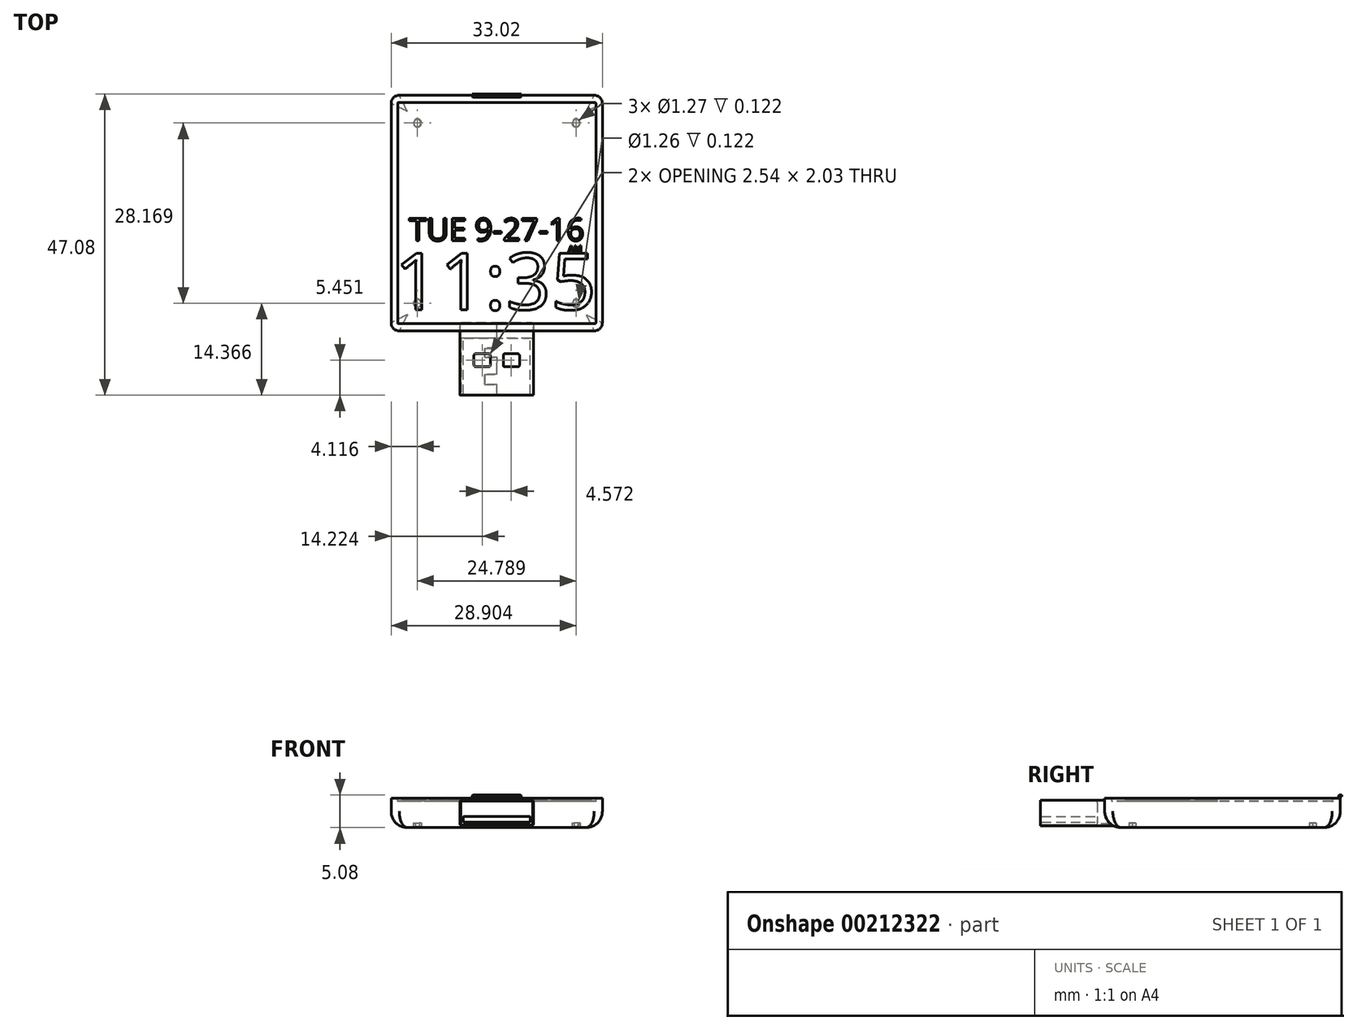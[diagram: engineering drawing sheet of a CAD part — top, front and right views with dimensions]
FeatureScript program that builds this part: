
annotation { "Feature Type Name" : "Feature", "Feature Type Description" : "" }
export const myFeature = defineFeature(function(context is Context, id is Id, definition is map)
    precondition{}
    {
        {
            var Q0;
            Q0=qCreatedBy(makeId("Top.planeOp"),FACE);
            var sketch = newSketch(context, id + "F0", { "sketchPlane" : qUnion([Q0])});
            skLineSegment(sketch, "E0.bottom", {"start": v(16.51, 18.41) * mm, "end": v(-16.51, 18.41) * mm});
            skLineSegment(sketch, "E0.top", {"start": v(16.51, -18.41) * mm, "end": v(-16.51, -18.41) * mm});
            skLineSegment(sketch, "E0.left", {"start": v(16.51, 18.41) * mm, "end": v(16.51, -18.41) * mm});
            skLineSegment(sketch, "E0.right", {"start": v(-16.51, 18.41) * mm, "end": v(-16.51, -18.41) * mm});
            skPoint(sketch, "E0.middle", {"position": v(0, 0) * mm});
            skSolve(sketch);
        }
        {
            var Q0;
            Q0=makeQuery(id+"F0.imprint","IMPRINT",FACE,{"disambiguationData":[TD([[makeQuery(id+"F0.imprint","IMPRINT",EDGE,{"derivedFrom":sQuery(id+"F0.wireOp",EDGE,"E0.bottom")}),1.0]])]});
            extrude(context, id + "F1", {"entities" : qUnion([Q0]), "depth" : 4.57 * mm});
        }
        {
            var Q0;
            Q0=makeQuery(id+"F1.opExtrude","CAP_FACE",FACE,{"disambiguationData":[OSD([sQuery(id+"F0.wireOp",EDGE,"E0.bottom"),sQuery(id+"F0.wireOp",EDGE,"E0.top"),sQuery(id+"F0.wireOp",EDGE,"E0.left"),sQuery(id+"F0.wireOp",EDGE,"E0.right")])],"isStart":false});
            var sketch = newSketch(context, id + "F2", { "sketchPlane" : qUnion([Q0])});
            skLineSegment(sketch, "E1.bottom", {"start": v(15.5, 17.27) * mm, "end": v(-15.5, 17.27) * mm});
            skLineSegment(sketch, "E1.top", {"start": v(15.5, -17.27) * mm, "end": v(-15.5, -17.27) * mm});
            skLineSegment(sketch, "E1.left", {"start": v(15.5, 17.27) * mm, "end": v(15.5, -17.27) * mm});
            skLineSegment(sketch, "E1.right", {"start": v(-15.5, 17.27) * mm, "end": v(-15.5, -17.27) * mm});
            skPoint(sketch, "E1.middle", {"position": v(0, 0) * mm});
            skSolve(sketch);
        }
        {
            var Q0;
            Q0=makeQuery(id+"F2.imprint","IMPRINT",FACE,{"disambiguationData":[TD([[makeQuery(id+"F2.imprint","IMPRINT",EDGE,{"derivedFrom":sQuery(id+"F2.wireOp",EDGE,"E1.bottom")}),1.0]])]});
            extrude(context, id + "F3", {"entities" : qUnion([Q0]), "operationType" : NewBodyOperationType.REMOVE, "oppositeDirection" : true, "depth" : 0.5 * mm});
        }
        {
            var Q0;
            Q0=makeQuery(id+"F1.opExtrude","CAP_FACE",FACE,{"disambiguationData":[OSD([sQuery(id+"F0.wireOp",EDGE,"E0.bottom"),sQuery(id+"F0.wireOp",EDGE,"E0.top"),sQuery(id+"F0.wireOp",EDGE,"E0.left"),sQuery(id+"F0.wireOp",EDGE,"E0.right")])],"isStart":false});
            var sketch = newSketch(context, id + "F4", { "sketchPlane" : qUnion([Q0])});
            skLineSegment(sketch, "E2.bottom", {"start": v(3.81, 18.12) * mm, "end": v(-3.81, 18.12) * mm});
            skLineSegment(sketch, "E2.left", {"start": v(3.81, 18.12) * mm, "end": v(3.81, 18.41) * mm});
            skLineSegment(sketch, "E2.right", {"start": v(-3.81, 18.12) * mm, "end": v(-3.81, 18.41) * mm});
            skPoint(sketch, "E2.middle", {"position": v(0, 18.41) * mm});
            skLineSegment(sketch, "E3", {"start": v(-3.81, 18.41) * mm, "end": v(3.81, 18.41) * mm});
            skSolve(sketch);
        }
        {
            var Q0;
            Q0=makeQuery(id+"F4.imprint","IMPRINT",FACE,{"disambiguationData":[TD([[makeQuery(id+"F4.imprint","IMPRINT",EDGE,{"derivedFrom":sQuery(id+"F4.wireOp",EDGE,"E2.bottom")}),-1.0]])]});
            extrude(context, id + "F5", {"entities" : qUnion([Q0]), "operationType" : NewBodyOperationType.ADD, "depth" : 0.5 * mm});
        }
        {
            var Q0;
            Q0=makeQuery(id+"F5.boolean.opBoolean","MERGE",FACE,{"derivedFrom":[makeQuery(id+"F1.opExtrude","SWEPT_FACE",FACE,{"disambiguationData":[OSD([sQuery(id+"F0.wireOp",EDGE,"E0.bottom")])]}),makeQuery(id+"F5.opExtrude","SWEPT_FACE",FACE,{"disambiguationData":[OSD([sQuery(id+"F4.wireOp",EDGE,"E3")])]})]});
            var sketch = newSketch(context, id + "F6", { "sketchPlane" : qUnion([Q0])});
            skLineSegment(sketch, "E4.bottom", {"start": v(-3.81, 5.08) * mm, "end": v(3.81, 5.08) * mm});
            skLineSegment(sketch, "E4.top", {"start": v(-3.81, 4.83) * mm, "end": v(3.81, 4.83) * mm});
            skLineSegment(sketch, "E4.left", {"start": v(-3.81, 5.08) * mm, "end": v(-3.81, 4.83) * mm});
            skLineSegment(sketch, "E4.right", {"start": v(3.81, 5.08) * mm, "end": v(3.81, 4.83) * mm});
            skSolve(sketch);
        }
        {
            var Q0;
            Q0=makeQuery(id+"F6.imprint","IMPRINT",FACE,{"disambiguationData":[TD([[makeQuery(id+"F6.imprint","IMPRINT",EDGE,{"derivedFrom":sQuery(id+"F6.wireOp",EDGE,"E4.bottom")}),-1.0]])]});
            extrude(context, id + "F7", {"entities" : qUnion([Q0]), "operationType" : NewBodyOperationType.ADD, "depth" : 0.2 * mm});
        }
        {
            var Q0;
            Q0=makeQuery(id+"F5.opExtrude","CAP_EDGE",EDGE,{"disambiguationData":[OSD([sQuery(id+"F4.wireOp",EDGE,"E2.bottom")])],"isStart":false});
            var Q1;
            Q1=makeQuery(id+"F7.boolean.opBoolean","MERGE",EDGE,{"derivedFrom":[makeQuery(id+"F5.opExtrude","CAP_EDGE",EDGE,{"disambiguationData":[OSD([sQuery(id+"F4.wireOp",EDGE,"E2.left")])],"isStart":false}),makeQuery(id+"F7.opExtrude","SWEPT_EDGE",EDGE,{"disambiguationData":[OSD([sQuery(id+"F6.wireOp",EDGE,"E4.bottom"),sQuery(id+"F6.wireOp",EDGE,"E4.left")])]})]});
            var Q2;
            Q2=makeQuery(id+"F5.opExtrude","SWEPT_EDGE",EDGE,{"disambiguationData":[OSD([sQuery(id+"F4.wireOp",EDGE,"E2.bottom"),sQuery(id+"F4.wireOp",EDGE,"E2.left")])]});
            var Q3;
            Q3=makeQuery(id+"F7.boolean.opBoolean","MERGE",EDGE,{"derivedFrom":[makeQuery(id+"F5.opExtrude","CAP_EDGE",EDGE,{"disambiguationData":[OSD([sQuery(id+"F4.wireOp",EDGE,"E2.right")])],"isStart":false}),makeQuery(id+"F7.opExtrude","SWEPT_EDGE",EDGE,{"disambiguationData":[OSD([sQuery(id+"F6.wireOp",EDGE,"E4.bottom"),sQuery(id+"F6.wireOp",EDGE,"E4.right")])]})]});
            var Q4;
            Q4=makeQuery(id+"F5.opExtrude","SWEPT_EDGE",EDGE,{"disambiguationData":[OSD([sQuery(id+"F4.wireOp",EDGE,"E2.bottom"),sQuery(id+"F4.wireOp",EDGE,"E2.right")])]});
            chamfer(context, id + "F8", {"entities" : qUnion([Q0, Q1, Q2, Q3, Q4]), "width" : 0.13 * mm, "tangentPropagation" : true});
        }
        {
            var Q0;
            Q0=makeQuery(id+"F1.opExtrude","SWEPT_FACE",FACE,{"disambiguationData":[OSD([sQuery(id+"F0.wireOp",EDGE,"E0.top")])]});
            var sketch = newSketch(context, id + "F9", { "sketchPlane" : qUnion([Q0])});
            skLineSegment(sketch, "E5.bottom", {"start": v(5.74, 0.3) * mm, "end": v(-5.74, 0.3) * mm});
            skLineSegment(sketch, "E5.top", {"start": v(5.74, 4.27) * mm, "end": v(-5.74, 4.27) * mm});
            skLineSegment(sketch, "E5.left", {"start": v(5.74, 0.3) * mm, "end": v(5.74, 4.27) * mm});
            skLineSegment(sketch, "E5.right", {"start": v(-5.74, 0.3) * mm, "end": v(-5.74, 4.27) * mm});
            skPoint(sketch, "E5.middle", {"position": v(0, 2.29) * mm});
            skPoint(sketch, "E6.orphan", {"position": v(0, 4.57) * mm});
            skPoint(sketch, "E7.start.orphan", {"position": v(0, 0) * mm});
            skSolve(sketch);
        }
        {
            var Q0;
            Q0=makeQuery(id+"F9.imprint","IMPRINT",FACE,{"disambiguationData":[TD([[makeQuery(id+"F9.imprint","IMPRINT",EDGE,{"derivedFrom":sQuery(id+"F9.wireOp",EDGE,"E5.bottom")}),-1.0]])]});
            extrude(context, id + "F10", {"entities" : qUnion([Q0]), "operationType" : NewBodyOperationType.ADD, "depth" : 10.03 * mm});
        }
        {
            var Q0;
            Q0=makeQuery(id+"F10.opExtrude","CAP_FACE",FACE,{"disambiguationData":[OSD([sQuery(id+"F9.wireOp",EDGE,"E5.bottom"),sQuery(id+"F9.wireOp",EDGE,"E5.top"),sQuery(id+"F9.wireOp",EDGE,"E5.left"),sQuery(id+"F9.wireOp",EDGE,"E5.right")])],"isStart":false});
            var sketch = newSketch(context, id + "F11", { "sketchPlane" : qUnion([Q0])});
            skLineSegment(sketch, "E8", {"start": v(0, 4.27) * mm, "end": v(0, 4.15) * mm});
            skLineSegment(sketch, "E9.bottom", {"start": v(5.61, 4.15) * mm, "end": v(-5.61, 4.15) * mm});
            skLineSegment(sketch, "E9.top", {"start": v(5.61, 0.42) * mm, "end": v(-5.61, 0.42) * mm});
            skLineSegment(sketch, "E9.left", {"start": v(5.61, 4.15) * mm, "end": v(5.61, 0.42) * mm});
            skLineSegment(sketch, "E9.right", {"start": v(-5.61, 4.15) * mm, "end": v(-5.61, 0.42) * mm});
            skPoint(sketch, "E9.middle", {"position": v(0, 2.29) * mm});
            skLineSegment(sketch, "E10.trimOffspring", {"start": v(0, 0.42) * mm, "end": v(0, 0.3) * mm});
            skSolve(sketch);
        }
        {
            var Q0;
            {var subQ0=sQuery(id+"F11.wireOp",EDGE,"E9.left");Q0=makeQuery(id+"F11.imprint","IMPRINT",FACE,{"disambiguationData":[TD([[makeQuery(id+"F11.imprint","IMPRINT",EDGE,{"derivedFrom":subQ0}),-1.0]])]});}
            extrude(context, id + "F12", {"entities" : qUnion([Q0]), "operationType" : NewBodyOperationType.REMOVE, "oppositeDirection" : true, "depth" : 8.9 * mm});
        }
        {
            var Q0;
            Q0=makeQuery(id+"F10.opExtrude","SWEPT_EDGE",EDGE,{"disambiguationData":[OSD([sQuery(id+"F9.wireOp",EDGE,"E5.top"),sQuery(id+"F9.wireOp",EDGE,"E5.right")])]});
            var Q1;
            Q1=makeQuery(id+"F12.boolean.opBoolean","COPY",EDGE,{"derivedFrom":makeQuery(id+"F12.opExtrude","SWEPT_EDGE",EDGE,{"disambiguationData":[OSD([sQuery(id+"F11.wireOp",EDGE,"E9.bottom"),sQuery(id+"F11.wireOp",EDGE,"E9.right")])]})});
            var Q2;
            Q2=makeQuery(id+"F10.opExtrude","SWEPT_EDGE",EDGE,{"disambiguationData":[OSD([sQuery(id+"F9.wireOp",EDGE,"E5.top"),sQuery(id+"F9.wireOp",EDGE,"E5.left")])]});
            var Q3;
            Q3=makeQuery(id+"F12.boolean.opBoolean","COPY",EDGE,{"derivedFrom":makeQuery(id+"F12.opExtrude","SWEPT_EDGE",EDGE,{"disambiguationData":[OSD([sQuery(id+"F11.wireOp",EDGE,"E9.top"),sQuery(id+"F11.wireOp",EDGE,"E9.left")])]})});
            var Q4;
            Q4=makeQuery(id+"F12.boolean.opBoolean","COPY",EDGE,{"derivedFrom":makeQuery(id+"F12.opExtrude","SWEPT_EDGE",EDGE,{"disambiguationData":[OSD([sQuery(id+"F11.wireOp",EDGE,"E9.top"),sQuery(id+"F11.wireOp",EDGE,"E9.right")])]})});
            var Q5;
            Q5=makeQuery(id+"F10.opExtrude","SWEPT_EDGE",EDGE,{"disambiguationData":[OSD([sQuery(id+"F9.wireOp",EDGE,"E5.bottom"),sQuery(id+"F9.wireOp",EDGE,"E5.right")])]});
            var Q6;
            Q6=makeQuery(id+"F10.opExtrude","SWEPT_EDGE",EDGE,{"disambiguationData":[OSD([sQuery(id+"F9.wireOp",EDGE,"E5.bottom"),sQuery(id+"F9.wireOp",EDGE,"E5.left")])]});
            var Q7;
            Q7=makeQuery(id+"F12.boolean.opBoolean","COPY",EDGE,{"derivedFrom":makeQuery(id+"F12.opExtrude","SWEPT_EDGE",EDGE,{"disambiguationData":[OSD([sQuery(id+"F11.wireOp",EDGE,"E9.bottom"),sQuery(id+"F11.wireOp",EDGE,"E9.left")])]})});
            fillet(context, id + "F13", {"entities" : qUnion([Q0, Q1, Q2, Q3, Q4, Q5, Q6, Q7]), "radius" : 0.26 * mm, "tangentPropagation" : true, "allowEdgeOverflow" : false});
        }
        {
            var Q0;
            Q0=makeQuery(id+"F12.boolean.opBoolean","COPY",FACE,{"derivedFrom":makeQuery(id+"F12.opExtrude","CAP_FACE",FACE,{"disambiguationData":[OSD([sQuery(id+"F11.wireOp",EDGE,"E9.bottom"),sQuery(id+"F11.wireOp",EDGE,"E9.top"),sQuery(id+"F11.wireOp",EDGE,"E9.left"),sQuery(id+"F11.wireOp",EDGE,"E9.right")])],"isStart":false})});
            var sketch = newSketch(context, id + "F14", { "sketchPlane" : qUnion([Q0])});
            skLineSegment(sketch, "E11.bottom", {"start": v(-5.22, 1.74) * mm, "end": v(5.22, 1.74) * mm});
            skLineSegment(sketch, "E11.top", {"start": v(-5.22, 0.86) * mm, "end": v(5.22, 0.86) * mm});
            skLineSegment(sketch, "E11.left", {"start": v(-5.22, 1.74) * mm, "end": v(-5.22, 0.86) * mm});
            skLineSegment(sketch, "E11.right", {"start": v(5.22, 1.74) * mm, "end": v(5.22, 0.86) * mm});
            skSolve(sketch);
        }
        {
            var Q0;
            Q0=makeQuery(id+"F14.imprint","IMPRINT",FACE,{"disambiguationData":[TD([[makeQuery(id+"F14.imprint","IMPRINT",EDGE,{"derivedFrom":sQuery(id+"F14.wireOp",EDGE,"E11.bottom")}),-1.0]])]});
            extrude(context, id + "F15", {"entities" : qUnion([Q0]), "operationType" : NewBodyOperationType.ADD, "depth" : 8.9 * mm});
        }
        {
            var Q0;
            Q0=makeQuery(id+"F10.opExtrude","SWEPT_FACE",FACE,{"disambiguationData":[OSD([sQuery(id+"F9.wireOp",EDGE,"E5.top")])]});
            var sketch = newSketch(context, id + "F16", { "sketchPlane" : qUnion([Q0])});
            skLineSegment(sketch, "E12.bottom", {"start": v(-3.56, -21.98) * mm, "end": v(-1.02, -21.98) * mm});
            skLineSegment(sketch, "E12.top", {"start": v(-3.56, -24.02) * mm, "end": v(-1.02, -24.02) * mm});
            skLineSegment(sketch, "E12.left", {"start": v(-3.56, -21.98) * mm, "end": v(-3.56, -24.02) * mm});
            skLineSegment(sketch, "E12.right", {"start": v(-1.02, -21.98) * mm, "end": v(-1.02, -24.02) * mm});
            skLineSegment(sketch, "E13.bottom", {"start": v(1.02, -21.98) * mm, "end": v(3.56, -21.98) * mm});
            skLineSegment(sketch, "E13.top", {"start": v(1.02, -24.02) * mm, "end": v(3.56, -24.02) * mm});
            skLineSegment(sketch, "E13.left", {"start": v(1.02, -21.98) * mm, "end": v(1.02, -24.02) * mm});
            skLineSegment(sketch, "E13.right", {"start": v(3.56, -21.98) * mm, "end": v(3.56, -24.02) * mm});
            skSolve(sketch);
        }
        {
            var Q0;
            Q0=makeQuery(id+"F16.imprint","IMPRINT",FACE,{"disambiguationData":[TD([[makeQuery(id+"F16.imprint","IMPRINT",EDGE,{"derivedFrom":sQuery(id+"F16.wireOp",EDGE,"E13.bottom")}),-1.0]])]});
            var Q1;
            Q1=makeQuery(id+"F16.imprint","IMPRINT",FACE,{"disambiguationData":[TD([[makeQuery(id+"F16.imprint","IMPRINT",EDGE,{"derivedFrom":sQuery(id+"F16.wireOp",EDGE,"E12.bottom")}),-1.0]])]});
            extrude(context, id + "F17", {"entities" : qUnion([Q0, Q1]), "operationType" : NewBodyOperationType.REMOVE, "oppositeDirection" : true, "depth" : 0.33 * mm});
        }
        {
            var Q0;
            Q0=makeQuery(id+"F17.boolean.opBoolean","COPY",EDGE,{"derivedFrom":makeQuery(id+"F17.opExtrude","SWEPT_EDGE",EDGE,{"disambiguationData":[OSD([sQuery(id+"F16.wireOp",EDGE,"E13.bottom"),sQuery(id+"F16.wireOp",EDGE,"E13.left")])]})});
            var Q1;
            Q1=makeQuery(id+"F17.boolean.opBoolean","COPY",EDGE,{"derivedFrom":makeQuery(id+"F17.opExtrude","SWEPT_EDGE",EDGE,{"disambiguationData":[OSD([sQuery(id+"F16.wireOp",EDGE,"E12.bottom"),sQuery(id+"F16.wireOp",EDGE,"E12.left")])]})});
            var Q2;
            Q2=makeQuery(id+"F17.boolean.opBoolean","COPY",EDGE,{"derivedFrom":makeQuery(id+"F17.opExtrude","SWEPT_EDGE",EDGE,{"disambiguationData":[OSD([sQuery(id+"F16.wireOp",EDGE,"E12.bottom"),sQuery(id+"F16.wireOp",EDGE,"E12.right")])]})});
            var Q3;
            Q3=makeQuery(id+"F17.boolean.opBoolean","COPY",EDGE,{"derivedFrom":makeQuery(id+"F17.opExtrude","SWEPT_EDGE",EDGE,{"disambiguationData":[OSD([sQuery(id+"F16.wireOp",EDGE,"E13.bottom"),sQuery(id+"F16.wireOp",EDGE,"E13.right")])]})});
            var Q4;
            Q4=makeQuery(id+"F17.boolean.opBoolean","COPY",EDGE,{"derivedFrom":makeQuery(id+"F17.opExtrude","SWEPT_EDGE",EDGE,{"disambiguationData":[OSD([sQuery(id+"F16.wireOp",EDGE,"E13.top"),sQuery(id+"F16.wireOp",EDGE,"E13.right")])]})});
            var Q5;
            Q5=makeQuery(id+"F17.boolean.opBoolean","COPY",EDGE,{"derivedFrom":makeQuery(id+"F17.opExtrude","SWEPT_EDGE",EDGE,{"disambiguationData":[OSD([sQuery(id+"F16.wireOp",EDGE,"E12.top"),sQuery(id+"F16.wireOp",EDGE,"E12.right")])]})});
            var Q6;
            Q6=makeQuery(id+"F17.boolean.opBoolean","COPY",EDGE,{"derivedFrom":makeQuery(id+"F17.opExtrude","SWEPT_EDGE",EDGE,{"disambiguationData":[OSD([sQuery(id+"F16.wireOp",EDGE,"E12.top"),sQuery(id+"F16.wireOp",EDGE,"E12.left")])]})});
            var Q7;
            Q7=makeQuery(id+"F17.boolean.opBoolean","COPY",EDGE,{"derivedFrom":makeQuery(id+"F17.opExtrude","SWEPT_EDGE",EDGE,{"disambiguationData":[OSD([sQuery(id+"F16.wireOp",EDGE,"E13.top"),sQuery(id+"F16.wireOp",EDGE,"E13.left")])]})});
            fillet(context, id + "F18", {"entities" : qUnion([Q0, Q1, Q2, Q3, Q4, Q5, Q6, Q7]), "radius" : 0.25 * mm, "tangentPropagation" : true, "allowEdgeOverflow" : false});
        }
        {
            var Q0;
            Q0=makeQuery(id+"F15.opExtrude","SWEPT_EDGE",EDGE,{"disambiguationData":[OSD([sQuery(id+"F14.wireOp",EDGE,"E11.bottom"),sQuery(id+"F14.wireOp",EDGE,"E11.left")])]});
            var Q1;
            Q1=makeQuery(id+"F15.opExtrude","SWEPT_EDGE",EDGE,{"disambiguationData":[OSD([sQuery(id+"F14.wireOp",EDGE,"E11.bottom"),sQuery(id+"F14.wireOp",EDGE,"E11.right")])]});
            var Q2;
            Q2=makeQuery(id+"F15.opExtrude","SWEPT_EDGE",EDGE,{"disambiguationData":[OSD([sQuery(id+"F14.wireOp",EDGE,"E11.top"),sQuery(id+"F14.wireOp",EDGE,"E11.right")])]});
            var Q3;
            Q3=makeQuery(id+"F15.opExtrude","SWEPT_EDGE",EDGE,{"disambiguationData":[OSD([sQuery(id+"F14.wireOp",EDGE,"E11.top"),sQuery(id+"F14.wireOp",EDGE,"E11.left")])]});
            var Q4;
            Q4=makeQuery(id+"F15.opExtrude","CAP_EDGE",EDGE,{"disambiguationData":[OSD([sQuery(id+"F14.wireOp",EDGE,"E11.bottom")])],"isStart":false});
            var Q5;
            Q5=makeQuery(id+"F15.opExtrude","CAP_EDGE",EDGE,{"disambiguationData":[OSD([sQuery(id+"F14.wireOp",EDGE,"E11.top")])],"isStart":false});
            var Q6;
            Q6=makeQuery(id+"F15.opExtrude","CAP_EDGE",EDGE,{"disambiguationData":[OSD([sQuery(id+"F14.wireOp",EDGE,"E11.left")])],"isStart":false});
            var Q7;
            Q7=makeQuery(id+"F15.opExtrude","CAP_EDGE",EDGE,{"disambiguationData":[OSD([sQuery(id+"F14.wireOp",EDGE,"E11.right")])],"isStart":false});
            fillet(context, id + "F19", {"entities" : qUnion([Q0, Q1, Q2, Q3, Q4, Q5, Q6, Q7]), "radius" : 0.13 * mm, "tangentPropagation" : true, "allowEdgeOverflow" : false});
        }
        {
            var Q0;
            Q0=makeQuery(id+"F10.opExtrude","SWEPT_FACE",FACE,{"disambiguationData":[OSD([sQuery(id+"F9.wireOp",EDGE,"E5.bottom")])]});
            var sketch = newSketch(context, id + "F20", { "sketchPlane" : qUnion([Q0])});
            skLineSegment(sketch, "E14", {"start": v(0, 28.45) * mm, "end": v(0, 26.77) * mm});
            skLineSegment(sketch, "E15", {"start": v(0, 26.77) * mm, "end": v(-1.86, 26.77) * mm});
            skLineSegment(sketch, "E16", {"start": v(-1.86, 26.77) * mm, "end": v(-1.86, 25.2) * mm});
            skLineSegment(sketch, "E17", {"start": v(-1.86, 25.2) * mm, "end": v(0, 25.2) * mm});
            skLineSegment(sketch, "E18", {"start": v(0, 25.2) * mm, "end": v(0, 22.54) * mm});
            skLineSegment(sketch, "E19", {"start": v(0, 22.54) * mm, "end": v(-1.86, 22.54) * mm});
            skLineSegment(sketch, "E20", {"start": v(-1.86, 22.54) * mm, "end": v(-1.86, 21.11) * mm});
            skLineSegment(sketch, "E21", {"start": v(-1.86, 21.11) * mm, "end": v(0, 21.11) * mm});
            skLineSegment(sketch, "E22", {"start": v(0, 21.11) * mm, "end": v(0, 18.41) * mm});
            skLineSegment(sketch, "E23", {"start": v(0, 18.41) * mm, "end": v(0, 18.41) * mm});
            skLineSegment(sketch, "E24", {"start": v(0, 18.41) * mm, "end": v(0, 21.1) * mm});
            skLineSegment(sketch, "E25", {"start": v(0, 21.1) * mm, "end": v(-1.86, 21.1) * mm});
            skLineSegment(sketch, "E26", {"start": v(-1.86, 21.1) * mm, "end": v(-1.86, 22.54) * mm});
            skLineSegment(sketch, "E27", {"start": v(-1.86, 22.54) * mm, "end": v(0, 22.54) * mm});
            skLineSegment(sketch, "E28", {"start": v(0, 22.54) * mm, "end": v(0, 25.2) * mm});
            skLineSegment(sketch, "E29", {"start": v(0, 25.2) * mm, "end": v(-1.86, 25.2) * mm});
            skLineSegment(sketch, "E30", {"start": v(-1.86, 25.2) * mm, "end": v(-1.86, 26.77) * mm});
            skLineSegment(sketch, "E31", {"start": v(-1.86, 26.77) * mm, "end": v(0, 26.77) * mm});
            skLineSegment(sketch, "E32", {"start": v(0, 26.77) * mm, "end": v(0, 28.45) * mm});
            skLineSegment(sketch, "E33", {"start": v(0, 28.45) * mm, "end": v(0, 28.45) * mm});
            skSolve(sketch);
        }
        {
            var Q0;
            Q0=makeQuery(id+"F20.imprint","IMPRINT",FACE,{"disambiguationData":[TD([[makeQuery(id+"F20.imprint","IMPRINT",EDGE,{"derivedFrom":sQuery(id+"F20.wireOp",EDGE,"E14")}),-1.0]])]});
            extrude(context, id + "F21", {"entities" : qUnion([Q0]), "operationType" : NewBodyOperationType.REMOVE, "oppositeDirection" : true, "depth" : 0.27 * mm});
        }
        {
            var Q0;
            Q0=makeQuery(id+"F3.boolean.opBoolean","COPY",EDGE,{"derivedFrom":makeQuery(id+"F3.opExtrude","CAP_EDGE",EDGE,{"disambiguationData":[OSD([sQuery(id+"F2.wireOp",EDGE,"E1.top")])],"isStart":true})});
            var Q1;
            Q1=makeQuery(id+"F3.boolean.opBoolean","COPY",EDGE,{"derivedFrom":makeQuery(id+"F3.opExtrude","CAP_EDGE",EDGE,{"disambiguationData":[OSD([sQuery(id+"F2.wireOp",EDGE,"E1.left")])],"isStart":true})});
            var Q2;
            Q2=makeQuery(id+"F3.boolean.opBoolean","COPY",EDGE,{"derivedFrom":makeQuery(id+"F3.opExtrude","CAP_EDGE",EDGE,{"disambiguationData":[OSD([sQuery(id+"F2.wireOp",EDGE,"E1.bottom")])],"isStart":true})});
            var Q3;
            Q3=makeQuery(id+"F3.boolean.opBoolean","COPY",EDGE,{"derivedFrom":makeQuery(id+"F3.opExtrude","CAP_EDGE",EDGE,{"disambiguationData":[OSD([sQuery(id+"F2.wireOp",EDGE,"E1.right")])],"isStart":true})});
            var Q4;
            Q4=makeQuery(id+"F3.boolean.opBoolean","COPY",EDGE,{"derivedFrom":makeQuery(id+"F3.opExtrude","SWEPT_EDGE",EDGE,{"disambiguationData":[OSD([sQuery(id+"F2.wireOp",EDGE,"E1.bottom"),sQuery(id+"F2.wireOp",EDGE,"E1.right")])]})});
            var Q5;
            Q5=makeQuery(id+"F3.boolean.opBoolean","COPY",EDGE,{"derivedFrom":makeQuery(id+"F3.opExtrude","SWEPT_EDGE",EDGE,{"disambiguationData":[OSD([sQuery(id+"F2.wireOp",EDGE,"E1.top"),sQuery(id+"F2.wireOp",EDGE,"E1.right")])]})});
            var Q6;
            Q6=makeQuery(id+"F3.boolean.opBoolean","COPY",EDGE,{"derivedFrom":makeQuery(id+"F3.opExtrude","SWEPT_EDGE",EDGE,{"disambiguationData":[OSD([sQuery(id+"F2.wireOp",EDGE,"E1.top"),sQuery(id+"F2.wireOp",EDGE,"E1.left")])]})});
            var Q7;
            Q7=makeQuery(id+"F3.boolean.opBoolean","COPY",EDGE,{"derivedFrom":makeQuery(id+"F3.opExtrude","SWEPT_EDGE",EDGE,{"disambiguationData":[OSD([sQuery(id+"F2.wireOp",EDGE,"E1.bottom"),sQuery(id+"F2.wireOp",EDGE,"E1.left")])]})});
            fillet(context, id + "F22", {"entities" : qUnion([Q0, Q1, Q2, Q3, Q4, Q5, Q6, Q7]), "radius" : 0.1 * mm, "tangentPropagation" : true, "allowEdgeOverflow" : false});
        }
        {
            var Q0;
            Q0=makeQuery(id+"F1.opExtrude","CAP_EDGE",EDGE,{"disambiguationData":[OSD([sQuery(id+"F0.wireOp",EDGE,"E0.left")])],"isStart":true});
            var Q1;
            Q1=makeQuery(id+"F1.opExtrude","CAP_EDGE",EDGE,{"disambiguationData":[OSD([sQuery(id+"F0.wireOp",EDGE,"E0.top")])],"isStart":true});
            var Q2;
            Q2=makeQuery(id+"F1.opExtrude","CAP_EDGE",EDGE,{"disambiguationData":[OSD([sQuery(id+"F0.wireOp",EDGE,"E0.right")])],"isStart":true});
            var Q3;
            Q3=makeQuery(id+"F1.opExtrude","CAP_EDGE",EDGE,{"disambiguationData":[OSD([sQuery(id+"F0.wireOp",EDGE,"E0.bottom")])],"isStart":true});
            fillet(context, id + "F23", {"entities" : qUnion([Q0, Q1, Q2, Q3]), "radius" : 2.54 * mm, "tangentPropagation" : true, "allowEdgeOverflow" : false});
        }
        {
            var Q0;
            Q0=makeQuery(id+"F1.opExtrude","SWEPT_EDGE",EDGE,{"disambiguationData":[OSD([sQuery(id+"F0.wireOp",EDGE,"E0.bottom"),sQuery(id+"F0.wireOp",EDGE,"E0.right")])]});
            var Q1;
            Q1=makeQuery(id+"F1.opExtrude","SWEPT_EDGE",EDGE,{"disambiguationData":[OSD([sQuery(id+"F0.wireOp",EDGE,"E0.top"),sQuery(id+"F0.wireOp",EDGE,"E0.right")])]});
            var Q2;
            Q2=makeQuery(id+"F1.opExtrude","SWEPT_EDGE",EDGE,{"disambiguationData":[OSD([sQuery(id+"F0.wireOp",EDGE,"E0.top"),sQuery(id+"F0.wireOp",EDGE,"E0.left")])]});
            var Q3;
            Q3=makeQuery(id+"F1.opExtrude","SWEPT_EDGE",EDGE,{"disambiguationData":[OSD([sQuery(id+"F0.wireOp",EDGE,"E0.bottom"),sQuery(id+"F0.wireOp",EDGE,"E0.left")])]});
            fillet(context, id + "F24", {"entities" : qUnion([Q0, Q1, Q2, Q3]), "radius" : 1.27 * mm, "tangentPropagation" : true, "allowEdgeOverflow" : false});
        }
        {
            var Q0;
            Q0=makeQuery(id+"F1.opExtrude","CAP_FACE",FACE,{"disambiguationData":[OSD([sQuery(id+"F0.wireOp",EDGE,"E0.bottom"),sQuery(id+"F0.wireOp",EDGE,"E0.top"),sQuery(id+"F0.wireOp",EDGE,"E0.left"),sQuery(id+"F0.wireOp",EDGE,"E0.right")])],"isStart":true});
            var sketch = newSketch(context, id + "F25", { "sketchPlane" : qUnion([Q0])});
            skLineSegment(sketch, "E34", {"start": v(-12.4, 14.08) * mm, "end": v(-12.4, -14.08) * mm, "construction": true});
            skLineSegment(sketch, "E35", {"start": v(-12.4, -14.08) * mm, "end": v(12.4, -14.08) * mm, "construction": true});
            skLineSegment(sketch, "E36", {"start": v(12.4, -14.08) * mm, "end": v(12.4, 14.08) * mm, "construction": true});
            skLineSegment(sketch, "E37", {"start": v(12.4, 14.08) * mm, "end": v(-12.4, 14.08) * mm, "construction": true});
            skCircle(sketch, "E38", {"center": v(-12.4, 14.08) * mm, "radius": 0.63 * mm});
            skCircle(sketch, "E39", {"center": v(12.4, 14.08) * mm, "radius": 0.63 * mm});
            skCircle(sketch, "E40", {"center": v(12.4, -14.08) * mm, "radius": 0.63 * mm});
            skCircle(sketch, "E41", {"center": v(-12.4, -14.08) * mm, "radius": 0.63 * mm});
            skSolve(sketch);
        }
        {
            var Q0;
            Q0=makeQuery(id+"F25.imprint","IMPRINT",FACE,{"disambiguationData":[TD([[makeQuery(id+"F25.imprint","IMPRINT",EDGE,{"derivedFrom":sQuery(id+"F25.wireOp",EDGE,"E41")}),1.0]])]});
            var Q1;
            Q1=makeQuery(id+"F25.imprint","IMPRINT",FACE,{"disambiguationData":[TD([[makeQuery(id+"F25.imprint","IMPRINT",EDGE,{"derivedFrom":sQuery(id+"F25.wireOp",EDGE,"E40")}),1.0]])]});
            var Q2;
            Q2=makeQuery(id+"F25.imprint","IMPRINT",FACE,{"disambiguationData":[TD([[makeQuery(id+"F25.imprint","IMPRINT",EDGE,{"derivedFrom":sQuery(id+"F25.wireOp",EDGE,"E39")}),1.0]])]});
            var Q3;
            Q3=makeQuery(id+"F25.imprint","IMPRINT",FACE,{"disambiguationData":[TD([[makeQuery(id+"F25.imprint","IMPRINT",EDGE,{"derivedFrom":sQuery(id+"F25.wireOp",EDGE,"E38")}),1.0]])]});
            extrude(context, id + "F26", {"entities" : qUnion([Q0, Q1, Q2, Q3]), "operationType" : NewBodyOperationType.REMOVE, "oppositeDirection" : true, "depth" : 0.12 * mm});
        }
        {
            var Q0;
            Q0=makeQuery(id+"F26.boolean.opBoolean","COPY",FACE,{"derivedFrom":makeQuery(id+"F26.opExtrude","CAP_FACE",FACE,{"disambiguationData":[OSD([sQuery(id+"F25.wireOp",EDGE,"E41")])],"isStart":false})});
            var sketch = newSketch(context, id + "F27", { "sketchPlane" : qUnion([Q0])});
            skCircle(sketch, "E42.cCircle", {"center": v(-12.4, -14.08) * mm, "radius": 0.54 * mm, "construction": true});
            skLineSegment(sketch, "E42.0", {"start": v(-12.7, -13.55) * mm, "end": v(-12.08, -13.55) * mm});
            skLineSegment(sketch, "E42.1", {"start": v(-12.08, -13.55) * mm, "end": v(-11.77, -14.08) * mm});
            skLineSegment(sketch, "E42.2", {"start": v(-11.77, -14.08) * mm, "end": v(-12.08, -14.62) * mm});
            skLineSegment(sketch, "E42.3", {"start": v(-12.08, -14.62) * mm, "end": v(-12.7, -14.62) * mm});
            skLineSegment(sketch, "E42.4", {"start": v(-12.7, -14.62) * mm, "end": v(-13.02, -14.08) * mm});
            skLineSegment(sketch, "E42.5", {"start": v(-13.02, -14.08) * mm, "end": v(-12.7, -13.55) * mm});
            skPoint(sketch, "E42.0.midPoint", {"position": v(-12.4, -13.55) * mm});
            skLineSegment(sketch, "E43", {"start": v(12.4, -13.45) * mm, "end": v(12.4, -14.72) * mm});
            skCircle(sketch, "E44.cCircle", {"center": v(12.4, -14.08) * mm, "radius": 0.54 * mm, "construction": true});
            skLineSegment(sketch, "E44.0", {"start": v(12.09, -13.55) * mm, "end": v(12.7, -13.55) * mm});
            skLineSegment(sketch, "E44.1", {"start": v(12.7, -13.55) * mm, "end": v(13.02, -14.08) * mm});
            skLineSegment(sketch, "E44.2", {"start": v(13.02, -14.08) * mm, "end": v(12.7, -14.62) * mm});
            skLineSegment(sketch, "E44.3", {"start": v(12.7, -14.62) * mm, "end": v(12.09, -14.62) * mm});
            skLineSegment(sketch, "E44.4", {"start": v(12.09, -14.62) * mm, "end": v(11.78, -14.08) * mm});
            skLineSegment(sketch, "E44.5", {"start": v(11.78, -14.08) * mm, "end": v(12.09, -13.55) * mm});
            skPoint(sketch, "E44.0.midPoint", {"position": v(12.4, -13.55) * mm});
            skLineSegment(sketch, "E45", {"start": v(12.38, 14.72) * mm, "end": v(12.38, 13.46) * mm});
            skCircle(sketch, "E46.cCircle", {"center": v(12.38, 14.09) * mm, "radius": 0.52 * mm, "construction": true});
            skLineSegment(sketch, "E46.0", {"start": v(12.08, 14.61) * mm, "end": v(12.68, 14.61) * mm});
            skLineSegment(sketch, "E46.1", {"start": v(12.68, 14.61) * mm, "end": v(12.99, 14.09) * mm});
            skLineSegment(sketch, "E46.2", {"start": v(12.99, 14.09) * mm, "end": v(12.68, 13.56) * mm});
            skLineSegment(sketch, "E46.3", {"start": v(12.68, 13.56) * mm, "end": v(12.08, 13.56) * mm});
            skLineSegment(sketch, "E46.4", {"start": v(12.08, 13.56) * mm, "end": v(11.78, 14.09) * mm});
            skLineSegment(sketch, "E46.5", {"start": v(11.78, 14.09) * mm, "end": v(12.08, 14.61) * mm});
            skPoint(sketch, "E46.0.midPoint", {"position": v(12.38, 14.61) * mm});
            skCircle(sketch, "E47.cCircle", {"center": v(-12.4, 14.09) * mm, "radius": 0.55 * mm, "construction": true});
            skLineSegment(sketch, "E47.0", {"start": v(-12.7, 14.63) * mm, "end": v(-12.08, 14.63) * mm});
            skLineSegment(sketch, "E47.1", {"start": v(-12.08, 14.63) * mm, "end": v(-11.76, 14.09) * mm});
            skLineSegment(sketch, "E47.2", {"start": v(-11.76, 14.09) * mm, "end": v(-12.08, 13.54) * mm});
            skLineSegment(sketch, "E47.3", {"start": v(-12.08, 13.54) * mm, "end": v(-12.7, 13.54) * mm});
            skLineSegment(sketch, "E47.4", {"start": v(-12.7, 13.54) * mm, "end": v(-13.03, 14.09) * mm});
            skLineSegment(sketch, "E47.5", {"start": v(-13.03, 14.09) * mm, "end": v(-12.7, 14.63) * mm});
            skPoint(sketch, "E47.0.midPoint", {"position": v(-12.4, 14.63) * mm});
            skSolve(sketch);
        }
        {
            var Q0;
            Q0=makeQuery(id+"F27.imprint","IMPRINT",FACE,{"disambiguationData":[TD([[makeQuery(id+"F27.imprint","IMPRINT",EDGE,{"derivedFrom":sQuery(id+"F27.wireOp",EDGE,"E47.0")}),-1.0]])]});
            var Q1;
            {var subQ0=sQuery(id+"F27.wireOp",EDGE,"E46.4");Q1=makeQuery(id+"F27.imprint","IMPRINT",FACE,{"disambiguationData":[TD([[makeQuery(id+"F27.imprint","IMPRINT",EDGE,{"derivedFrom":subQ0}),-1.0]])]});}
            var Q2;
            {var subQ1=sQuery(id+"F27.wireOp",EDGE,"E46.1");Q2=makeQuery(id+"F27.imprint","IMPRINT",FACE,{"disambiguationData":[TD([[makeQuery(id+"F27.imprint","IMPRINT",EDGE,{"derivedFrom":subQ1}),-1.0]])]});}
            var Q3;
            {var subQ1=sQuery(id+"F27.wireOp",EDGE,"E44.1");Q3=makeQuery(id+"F27.imprint","IMPRINT",FACE,{"disambiguationData":[TD([[makeQuery(id+"F27.imprint","IMPRINT",EDGE,{"derivedFrom":subQ1}),-1.0]])]});}
            var Q4;
            {var subQ0=sQuery(id+"F27.wireOp",EDGE,"E44.4");Q4=makeQuery(id+"F27.imprint","IMPRINT",FACE,{"disambiguationData":[TD([[makeQuery(id+"F27.imprint","IMPRINT",EDGE,{"derivedFrom":subQ0}),-1.0]])]});}
            var Q5;
            Q5=makeQuery(id+"F27.imprint","IMPRINT",FACE,{"disambiguationData":[TD([[makeQuery(id+"F27.imprint","IMPRINT",EDGE,{"derivedFrom":sQuery(id+"F27.wireOp",EDGE,"E42.0")}),-1.0]])]});
            extrude(context, id + "F28", {"entities" : qUnion([Q0, Q1, Q2, Q3, Q4, Q5]), "operationType" : NewBodyOperationType.REMOVE, "oppositeDirection" : true, "depth" : 0.63 * mm});
        }
        {
            var Q0;
            Q0=makeQuery(id+"F3.boolean.opBoolean","COPY",FACE,{"derivedFrom":makeQuery(id+"F3.opExtrude","CAP_FACE",FACE,{"disambiguationData":[OSD([sQuery(id+"F2.wireOp",EDGE,"E1.bottom"),sQuery(id+"F2.wireOp",EDGE,"E1.top"),sQuery(id+"F2.wireOp",EDGE,"E1.left"),sQuery(id+"F2.wireOp",EDGE,"E1.right")])],"isStart":false})});
            extrude(context, id + "F29", {"entities" : qUnion([Q0]), "depth" : 0.1 * mm});
        }
        {
            var Q0;
            Q0=makeQuery(id+"F29.opExtrude","CAP_FACE",FACE,{"disambiguationData":[OSD([sQuery(id+"F2.wireOp",EDGE,"E1.bottom"),sQuery(id+"F2.wireOp",EDGE,"E1.top"),sQuery(id+"F2.wireOp",EDGE,"E1.left"),sQuery(id+"F2.wireOp",EDGE,"E1.right")])],"isStart":false});
            var sketch = newSketch(context, id + "F30", { "sketchPlane" : qUnion([Q0])});
            skText(sketch, "E48", { "text": "11:35", "fontName": "OpenSans-Regular.ttf"});
            skText(sketch, "E49", { "text": "TUE 9-27-16", "fontName": "OpenSans-Regular.ttf"});
            skText(sketch, "E50", { "text": "AM", "fontName": "OpenSans-Regular.ttf"});
            const initialGuessF30  = {"E48": [-0.016, -0.01508, 1, 0, 0.00889], "E49": [-0.0137, -0.00432, 1, 0, 0.00352], "E50": [0.0112, -0.00607, 1, 0, 0.00098]};
            skSetInitialGuess(sketch, initialGuessF30);
            skSolve(sketch);
        }
        {
            var Q0;
            Q0=makeQuery(id+"F30.imprint","IMPRINT",FACE,{"disambiguationData":[TD([[makeQuery(id+"F30.imprint","IMPRINT",EDGE,{"derivedFrom":sQuery(id+"F30.wireOp",EDGE,"E48.sketch_text.stroke-9")}),-1.0]])]});
            var Q1;
            Q1=makeQuery(id+"F30.imprint","IMPRINT",FACE,{"disambiguationData":[TD([[makeQuery(id+"F30.imprint","IMPRINT",EDGE,{"derivedFrom":sQuery(id+"F30.wireOp",EDGE,"E48.sketch_text.stroke-0")}),-1.0]])]});
            var Q2;
            Q2=makeQuery(id+"F30.imprint","IMPRINT",FACE,{"disambiguationData":[TD([[makeQuery(id+"F30.imprint","IMPRINT",EDGE,{"derivedFrom":sQuery(id+"F30.wireOp",EDGE,"E48.sketch_text.stroke-32")}),-1.0]])]});
            var Q3;
            Q3=makeQuery(id+"F30.imprint","IMPRINT",FACE,{"disambiguationData":[TD([[makeQuery(id+"F30.imprint","IMPRINT",EDGE,{"derivedFrom":sQuery(id+"F30.wireOp",EDGE,"E48.sketch_text.stroke-60")}),-1.0]])]});
            var Q4;
            Q4=makeQuery(id+"F30.imprint","IMPRINT",FACE,{"disambiguationData":[TD([[makeQuery(id+"F30.imprint","IMPRINT",EDGE,{"derivedFrom":sQuery(id+"F30.wireOp",EDGE,"E48.sketch_text.stroke-18")}),-1.0]])]});
            var Q5;
            Q5=makeQuery(id+"F30.imprint","IMPRINT",FACE,{"disambiguationData":[TD([[makeQuery(id+"F30.imprint","IMPRINT",EDGE,{"derivedFrom":sQuery(id+"F30.wireOp",EDGE,"E48.sketch_text.stroke-26")}),-1.0]])]});
            var Q6;
            Q6=makeQuery(id+"F30.imprint","IMPRINT",FACE,{"disambiguationData":[TD([[makeQuery(id+"F30.imprint","IMPRINT",EDGE,{"derivedFrom":sQuery(id+"F30.wireOp",EDGE,"E49.sketch_text.stroke-0")}),-1.0]])]});
            var Q7;
            Q7=makeQuery(id+"F30.imprint","IMPRINT",FACE,{"disambiguationData":[TD([[makeQuery(id+"F30.imprint","IMPRINT",EDGE,{"derivedFrom":sQuery(id+"F30.wireOp",EDGE,"E49.sketch_text.stroke-8")}),-1.0]])]});
            var Q8;
            Q8=makeQuery(id+"F30.imprint","IMPRINT",FACE,{"disambiguationData":[TD([[makeQuery(id+"F30.imprint","IMPRINT",EDGE,{"derivedFrom":sQuery(id+"F30.wireOp",EDGE,"E49.sketch_text.stroke-22")}),-1.0]])]});
            var Q9;
            Q9=makeQuery(id+"F30.imprint","IMPRINT",FACE,{"disambiguationData":[TD([[makeQuery(id+"F30.imprint","IMPRINT",EDGE,{"derivedFrom":sQuery(id+"F30.wireOp",EDGE,"E49.sketch_text.stroke-34")}),-1.0]])]});
            var Q10;
            Q10=makeQuery(id+"F30.imprint","IMPRINT",FACE,{"disambiguationData":[TD([[makeQuery(id+"F30.imprint","IMPRINT",EDGE,{"derivedFrom":sQuery(id+"F30.wireOp",EDGE,"E49.sketch_text.stroke-60")}),-1.0]])]});
            var Q11;
            Q11=makeQuery(id+"F30.imprint","IMPRINT",FACE,{"disambiguationData":[TD([[makeQuery(id+"F30.imprint","IMPRINT",EDGE,{"derivedFrom":sQuery(id+"F30.wireOp",EDGE,"E49.sketch_text.stroke-64")}),-1.0]])]});
            var Q12;
            Q12=makeQuery(id+"F30.imprint","IMPRINT",FACE,{"disambiguationData":[TD([[makeQuery(id+"F30.imprint","IMPRINT",EDGE,{"derivedFrom":sQuery(id+"F30.wireOp",EDGE,"E49.sketch_text.stroke-84")}),-1.0]])]});
            var Q13;
            Q13=makeQuery(id+"F30.imprint","IMPRINT",FACE,{"disambiguationData":[TD([[makeQuery(id+"F30.imprint","IMPRINT",EDGE,{"derivedFrom":sQuery(id+"F30.wireOp",EDGE,"E49.sketch_text.stroke-91")}),-1.0]])]});
            var Q14;
            Q14=makeQuery(id+"F30.imprint","IMPRINT",FACE,{"disambiguationData":[TD([[makeQuery(id+"F30.imprint","IMPRINT",EDGE,{"derivedFrom":sQuery(id+"F30.wireOp",EDGE,"E49.sketch_text.stroke-95")}),-1.0]])]});
            var Q15;
            Q15=makeQuery(id+"F30.imprint","IMPRINT",FACE,{"disambiguationData":[TD([[makeQuery(id+"F30.imprint","IMPRINT",EDGE,{"derivedFrom":sQuery(id+"F30.wireOp",EDGE,"E49.sketch_text.stroke-104")}),-1.0]])]});
            var Q16;
            Q16=makeQuery(id+"F30.imprint","IMPRINT",FACE,{"disambiguationData":[TD([[makeQuery(id+"F30.imprint","IMPRINT",EDGE,{"derivedFrom":sQuery(id+"F30.wireOp",EDGE,"E50.sketch_text.stroke-0")}),-1.0]])]});
            var Q17;
            Q17=makeQuery(id+"F30.imprint","IMPRINT",FACE,{"disambiguationData":[TD([[makeQuery(id+"F30.imprint","IMPRINT",EDGE,{"derivedFrom":sQuery(id+"F30.wireOp",EDGE,"E50.sketch_text.stroke-13")}),-1.0]])]});
            extrude(context, id + "F31", {"entities" : qUnion([Q0, Q1, Q2, Q3, Q4, Q5, Q6, Q7, Q8, Q9, Q10, Q11, Q12, Q13, Q14, Q15, Q16, Q17]), "operationType" : NewBodyOperationType.ADD, "depth" : 0.03 * mm});
        }
    });
